# Revit family: Faucet-Bidet-KOHLER-Purist-14434W_1
name_source: partatom
category: Plumbing Fixtures
revit_build: Autodesk Revit 2017 (Build: 20160225_1515(x64)
units: mm (PartAtom-declared; Revit-internal decimal feet)

## family parameters
Cut with Voids When Loaded = No
Host = Face
OmniClass Number = 23.31.11.00
OmniClass Title = Faucets
Part Type = Normal
Room Calculation Point = No
Round Connector Dimension = Use Diameter
Shared = No

## types (2) — shared parameters
ADA Compliant = No
Assembly Code = D2010
CW Connection = Yes
Cold Water Inlet = Cold Water Inlet
Date Modified = 07/28/2020
Default Elevation = 36"
Drain Included = Yes
Finish = Kohler-Metal-CP-Polished_Chrome
Flow Rate = 0 GPM
HW Connection = Yes
Height = 8"
Hot Water Inlet = Hot Water Inlet
Length = 4 1/4"
Manufacturer = KOHLER Co.
Master Format 2014 = 22.41.39
Master Format 2014 Name = Residential Faucets, Supplies, and Trim
Material = Brass Construction
Pressure = 0.00 psi
Product Name = Purist
Product Page URL = https://www.kohler.co.uk
Spout Reach = 4 1/4"
URL = https://www.kohler.co.uk
Vent Connection = No
Waste Connection = No
Waste Water Outlet = Waste Water Outlet
WaterSense Certified = No
Width = 2 1/4"

## per-type parameters (varying)
| type | Description | Handle Clearance | Model | Smile Handle | Straight Handle | Type |
| Straight Handle, CP-Polished Chrome | Single-lever monobloc bidet mixer, straight handle | 3 1/8" | 14434W-4A-CP | No | Yes | 2 |
| Smile Handle, CP-Polished Chrome | Single-lever monobloc bidet mixer, smile handle | 3 1/16" | 14434W-4-CP | Yes | No | 1 |

## geometry (parser evidence)
native form markers: Sweep x4
no freeform markers — native parametric forms only
